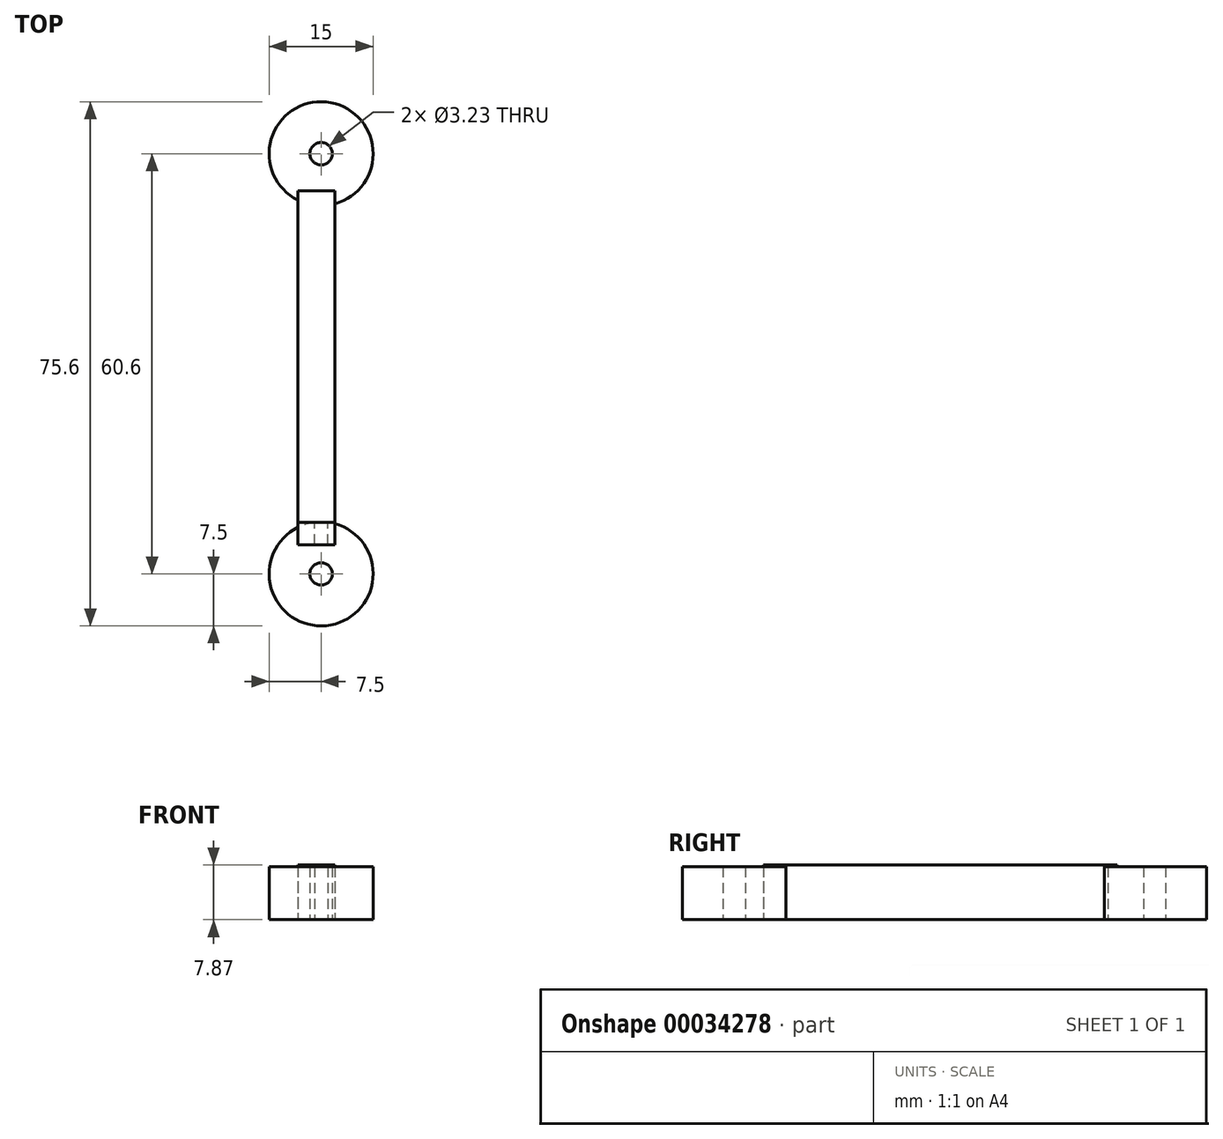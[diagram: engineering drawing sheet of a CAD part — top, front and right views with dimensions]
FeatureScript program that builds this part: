
annotation { "Feature Type Name" : "Feature", "Feature Type Description" : "" }
export const myFeature = defineFeature(function(context is Context, id is Id, definition is map)
    precondition{}
    {
        {
            var Q0;
            Q0=qCreatedBy(makeId("Top.planeOp"),FACE);
            var sketch = newSketch(context, id + "F0", { "sketchPlane" : qUnion([Q0])});
            skCircle(sketch, "E0", {"center": v(0, 0) * mm, "radius": 1.61 * mm});
            skCircle(sketch, "E1", {"center": v(0, 0) * mm, "radius": 7.5 * mm});
            skSolve(sketch);
        }
        {
            var Q0;
            Q0=makeQuery(id+"F0.imprint","IMPRINT",FACE,{"disambiguationData":[TD([[makeQuery(id+"F0.imprint","IMPRINT",EDGE,{"derivedFrom":sQuery(id+"F0.wireOp",EDGE,"E0")}),-1.0]])]});
            extrude(context, id + "F1", {"entities" : qUnion([Q0]), "depth" : 7.62 * mm, "offsetDistance" : 25.4 * mm});
        }
        {
            var Q0;
            Q0=qCreatedBy(makeId("Top.planeOp"),FACE);
            var sketch = newSketch(context, id + "F2", { "sketchPlane" : qUnion([Q0])});
            skLineSegment(sketch, "E2.bottom", {"start": v(2, -7.44) * mm, "end": v(-3.37, -7.44) * mm});
            skLineSegment(sketch, "E2.top", {"start": v(2, -53.16) * mm, "end": v(-3.37, -53.16) * mm});
            skLineSegment(sketch, "E2.left", {"start": v(2, -7.44) * mm, "end": v(2, -53.16) * mm});
            skLineSegment(sketch, "E2.right", {"start": v(-3.37, -7.44) * mm, "end": v(-3.37, -53.16) * mm});
            skSolve(sketch);
        }
        {
            var Q0;
            Q0=makeQuery(id+"F2.imprint","IMPRINT",FACE,{"disambiguationData":[TD([[makeQuery(id+"F2.imprint","IMPRINT",EDGE,{"derivedFrom":sQuery(id+"F2.wireOp",EDGE,"E2.bottom")}),1.0]])]});
            extrude(context, id + "F3", {"entities" : qUnion([Q0]), "depth" : 7.87 * mm, "offsetDistance" : 25.4 * mm});
        }
        {
            var Q0;
            Q0=makeQuery(id+"F3.opExtrude","CAP_EDGE",EDGE,{"disambiguationData":[OSD([sQuery(id+"F2.wireOp",EDGE,"E2.left")])],"isStart":true});
            cPoint(context, id + "F4", {"entities" : qUnion([Q0]), "parameter" : 0.5});
        }
        {
            var Q0;
            Q0=qCreatedBy(makeId("Front.planeOp"),FACE);
            var Q1;
            Q1 = qCreatedBy(id + "F4" ,VERTEX);
            cPlane(context, id + "F5", {"entities" : qUnion([Q0, Q1]), "cplaneType" : CPlaneType.PLANE_POINT, "offset" : 25.4 * mm, "width" : 152.4 * mm, "height" : 152.4 * mm});
        }
        {
            var Q0;
            Q0=makeQuery(id+"F1.opExtrude","SWEPT_BODY",BODY,{"disambiguationData":[OSD([sQuery(id+"F0.wireOp",EDGE,"E0"),sQuery(id+"F0.wireOp",EDGE,"E1")])]});
            var Q1;
            Q1=qCreatedBy(id+"F5.planeOp",FACE);
            mirror(context, id + "F6", {"operationType" : NewBodyOperationType.ADD, "entities" : qUnion([Q0]), "mirrorPlane" : qUnion([Q1])});
        }
        {
            var Q0;
            Q0=makeQuery(id+"F3.opExtrude","SWEPT_FACE",FACE,{"disambiguationData":[OSD([sQuery(id+"F2.wireOp",EDGE,"E2.top")])]});
            extrude(context, id + "F7", {"entities" : qUnion([Q0]), "depth" : 3.23 * mm, "offsetDistance" : 25.4 * mm});
        }
        {
            var Q0;
            Q0=makeQuery(id+"F3.opExtrude","SWEPT_FACE",FACE,{"disambiguationData":[OSD([sQuery(id+"F2.wireOp",EDGE,"E2.bottom")])]});
            extrude(context, id + "F8", {"entities" : qUnion([Q0]), "operationType" : NewBodyOperationType.ADD, "depth" : 2.06 * mm, "offsetDistance" : 25.4 * mm});
        }
    });
